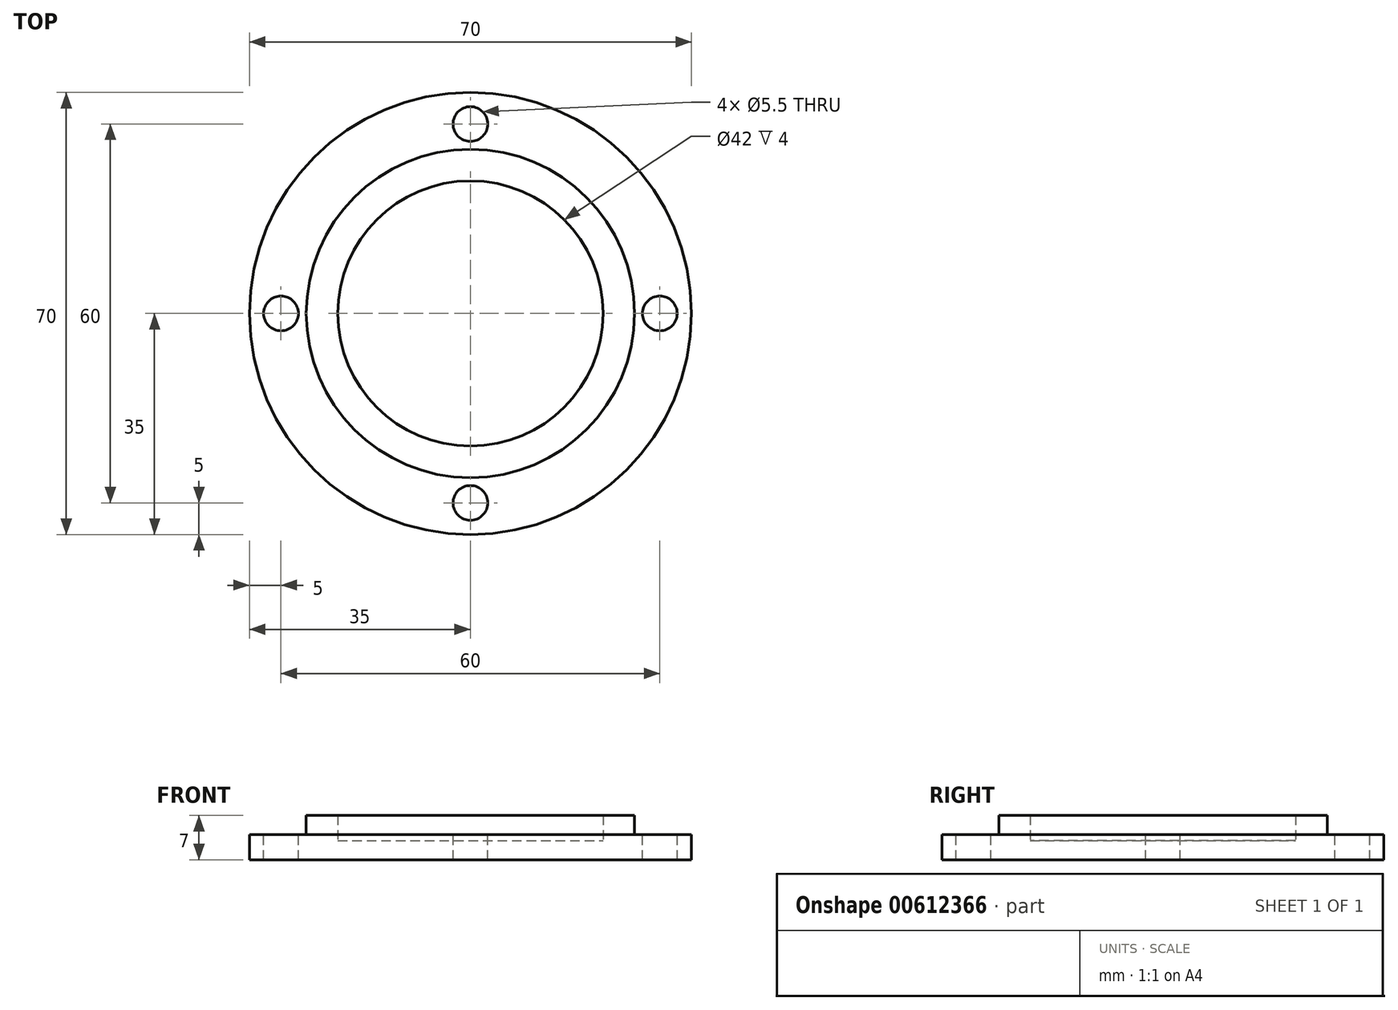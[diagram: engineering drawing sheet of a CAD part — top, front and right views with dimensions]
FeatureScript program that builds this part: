
annotation { "Feature Type Name" : "Feature", "Feature Type Description" : "" }
export const myFeature = defineFeature(function(context is Context, id is Id, definition is map)
    precondition{}
    {
        {
            var Q0;
            Q0=qCreatedBy(makeId("Front.planeOp"),FACE);
            var sketch = newSketch(context, id + "F0", { "sketchPlane" : qUnion([Q0])});
            skLineSegment(sketch, "E0", {"start": v(0, 0) * mm, "end": v(0, 43.17) * mm});
            skLineSegment(sketch, "E1", {"start": v(0, 0) * mm, "end": v(35, 0) * mm});
            skLineSegment(sketch, "E2", {"start": v(35, 0) * mm, "end": v(35, 4) * mm});
            skLineSegment(sketch, "E3", {"start": v(35, 4) * mm, "end": v(26, 4) * mm});
            skLineSegment(sketch, "E4", {"start": v(26, 4) * mm, "end": v(26, 7) * mm});
            skLineSegment(sketch, "E5", {"start": v(26, 7) * mm, "end": v(21, 7) * mm});
            skLineSegment(sketch, "E6", {"start": v(21, 7) * mm, "end": v(21, 3) * mm});
            skLineSegment(sketch, "E7", {"start": v(21, 3) * mm, "end": v(0, 3) * mm});
            skLineSegment(sketch, "E8", {"start": v(0, 3) * mm, "end": v(0, 0) * mm});
            skSolve(sketch);
        }
        {
            var Q0;
            Q0=makeQuery(id+"F0.imprint","IMPRINT",FACE,{"disambiguationData":[TD([[makeQuery(id+"F0.imprint","IMPRINT",EDGE,{"derivedFrom":sQuery(id+"F0.wireOp",EDGE,"E1")}),1.0]])]});
            var Q1;
            Q1=sQuery(id+"F0.wireOp",EDGE,"E0");
            revolve(context, id + "F1", {"entities" : qUnion([Q0]), "axis" : qUnion([Q1]), "revolveType" : RevolveType.FULL});
        }
        {
            var Q0;
            Q0=makeQuery(id+"F1.opRevolve","SWEPT_FACE",FACE,{"disambiguationData":[OSD([sQuery(id+"F0.wireOp",EDGE,"E3")])]});
            var sketch = newSketch(context, id + "F2", { "sketchPlane" : qUnion([Q0])});
            skArc(sketch, "E9", {"start": v(-2.75, 29.87) * mm, "mid": v(-21.21, 21.21) * mm, "end": v(-29.87, 2.75) * mm});
            skCircle(sketch, "E10", {"center": v(30, 0) * mm, "radius": 2.75 * mm});
            skCircle(sketch, "E11.1.0", {"center": v(0, 30) * mm, "radius": 2.75 * mm});
            skCircle(sketch, "E11.2.0", {"center": v(-30, 0) * mm, "radius": 2.75 * mm});
            skCircle(sketch, "E11.3.0", {"center": v(0, -30) * mm, "radius": 2.75 * mm});
            skArc(sketch, "E12.trimOffspring", {"start": v(-29.87, -2.75) * mm, "mid": v(-21.21, -21.21) * mm, "end": v(-2.75, -29.87) * mm});
            skArc(sketch, "E13.trimOffspring", {"start": v(2.75, -29.87) * mm, "mid": v(21.21, -21.21) * mm, "end": v(29.87, -2.75) * mm});
            skArc(sketch, "E14.trimOffspring", {"start": v(29.87, 2.75) * mm, "mid": v(21.21, 21.21) * mm, "end": v(2.75, 29.87) * mm});
            skSolve(sketch);
        }
        {
            var Q0;
            {var subQ0=sQuery(id+"F2.wireOp",EDGE,"E11.1.0");var subQ1=makeQuery(id+"F2.imprint","INTERSECT",VERTEX,{"derivedFrom":[sQuery(id+"F2.wireOp",EDGE,"E9"),subQ0]});Q0=makeQuery(id+"F2.imprint","IMPRINT",FACE,{"disambiguationData":[TD([[makeQuery(id+"F2.imprint","IMPRINT",EDGE,{"disambiguationData":[TD([[subQ1,-1.0]])],"derivedFrom":subQ0}),1.0]])]});}
            var Q1;
            {var subQ0=sQuery(id+"F2.wireOp",EDGE,"E11.2.0");var subQ1=makeQuery(id+"F2.imprint","INTERSECT",VERTEX,{"derivedFrom":[sQuery(id+"F2.wireOp",EDGE,"E9"),subQ0]});Q1=makeQuery(id+"F2.imprint","IMPRINT",FACE,{"disambiguationData":[TD([[makeQuery(id+"F2.imprint","IMPRINT",EDGE,{"disambiguationData":[TD([[subQ1,1.0]])],"derivedFrom":subQ0}),1.0]])]});}
            var Q2;
            {var subQ0=sQuery(id+"F2.wireOp",EDGE,"E11.3.0");var subQ1=makeQuery(id+"F2.imprint","INTERSECT",VERTEX,{"derivedFrom":[subQ0,sQuery(id+"F2.wireOp",EDGE,"E12.trimOffspring")]});Q2=makeQuery(id+"F2.imprint","IMPRINT",FACE,{"disambiguationData":[TD([[makeQuery(id+"F2.imprint","IMPRINT",EDGE,{"disambiguationData":[TD([[subQ1,1.0]])],"derivedFrom":subQ0}),1.0]])]});}
            var Q3;
            {var subQ0=sQuery(id+"F2.wireOp",EDGE,"E10");var subQ1=makeQuery(id+"F2.imprint","INTERSECT",VERTEX,{"derivedFrom":[subQ0,sQuery(id+"F2.wireOp",EDGE,"E13.trimOffspring")]});Q3=makeQuery(id+"F2.imprint","IMPRINT",FACE,{"disambiguationData":[TD([[makeQuery(id+"F2.imprint","IMPRINT",EDGE,{"disambiguationData":[TD([[subQ1,1.0]])],"derivedFrom":subQ0}),1.0]])]});}
            extrude(context, id + "F3", {"entities" : qUnion([Q0, Q1, Q2, Q3]), "operationType" : NewBodyOperationType.REMOVE, "oppositeDirection" : true, "depth" : 4 * mm, "offsetDistance" : 25 * mm});
        }
    });
